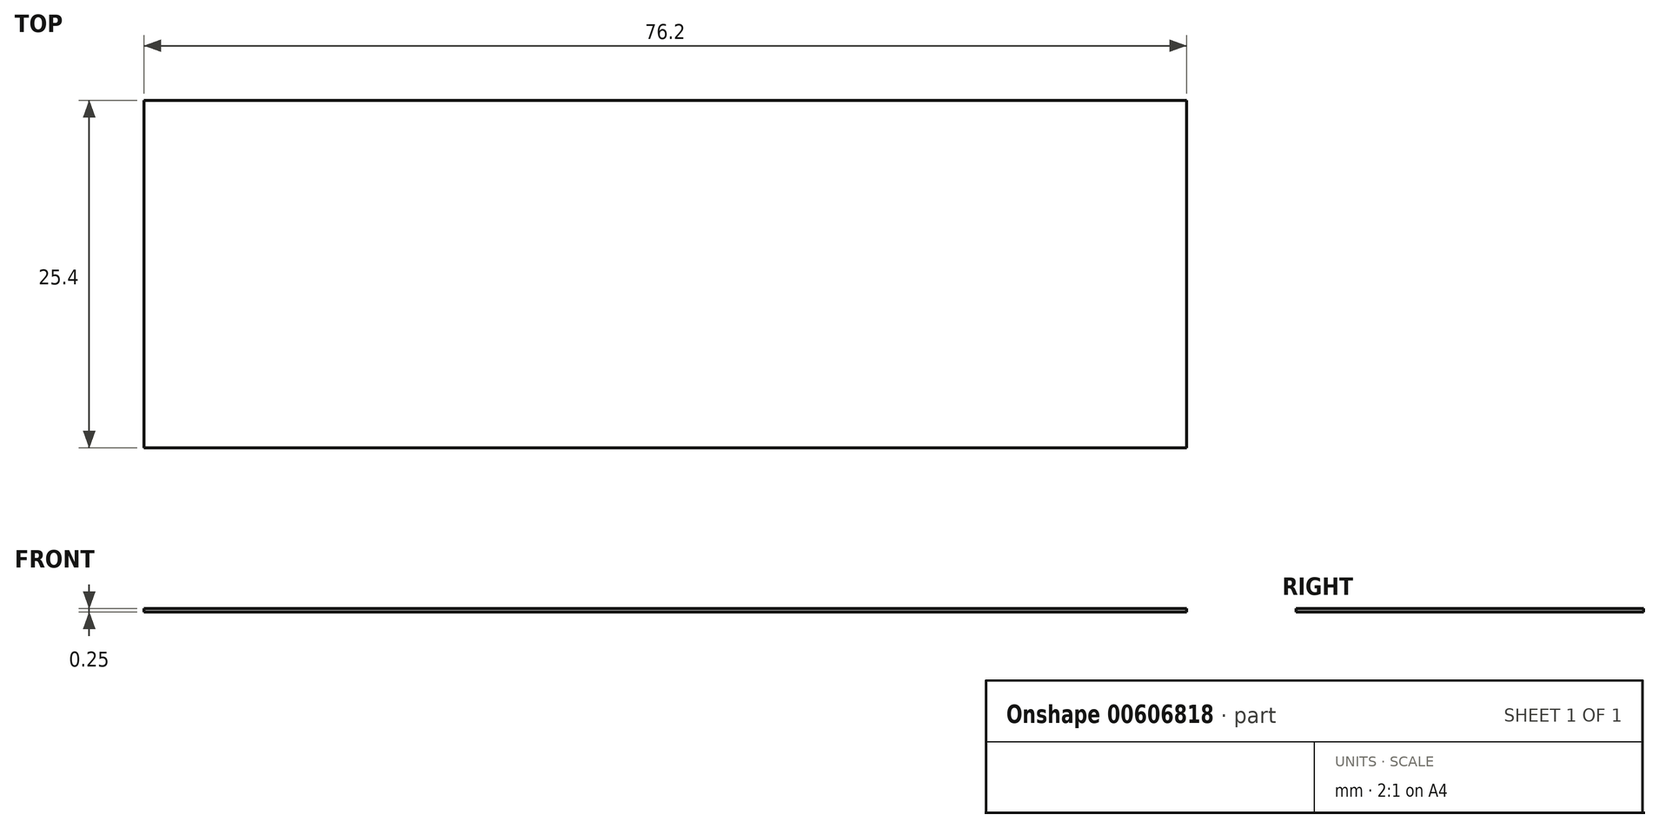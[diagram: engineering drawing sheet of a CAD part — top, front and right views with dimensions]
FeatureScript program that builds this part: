
annotation { "Feature Type Name" : "Feature", "Feature Type Description" : "" }
export const myFeature = defineFeature(function(context is Context, id is Id, definition is map)
    precondition{}
    {
        {
            var Q0;
            Q0=qCreatedBy(makeId("Top.planeOp"),FACE);
            var sketch = newSketch(context, id + "F0", { "sketchPlane" : qUnion([Q0])});
            skLineSegment(sketch, "E0.bottom", {"start": v(38.1, 12.7) * mm, "end": v(-38.1, 12.7) * mm});
            skLineSegment(sketch, "E0.top", {"start": v(38.1, -12.7) * mm, "end": v(-38.1, -12.7) * mm});
            skLineSegment(sketch, "E0.left", {"start": v(38.1, 12.7) * mm, "end": v(38.1, -12.7) * mm});
            skLineSegment(sketch, "E0.right", {"start": v(-38.1, 12.7) * mm, "end": v(-38.1, -12.7) * mm});
            skPoint(sketch, "E0.middle", {"position": v(0, 0) * mm});
            skSolve(sketch);
        }
        {
            var Q0;
            Q0 = qSketchRegion(id + "F0", true);
            extrude(context, id + "F1", {"entities" : qUnion([Q0]), "depth" : 0.25 * mm, "offsetDistance" : 25.4 * mm});
        }
    });
